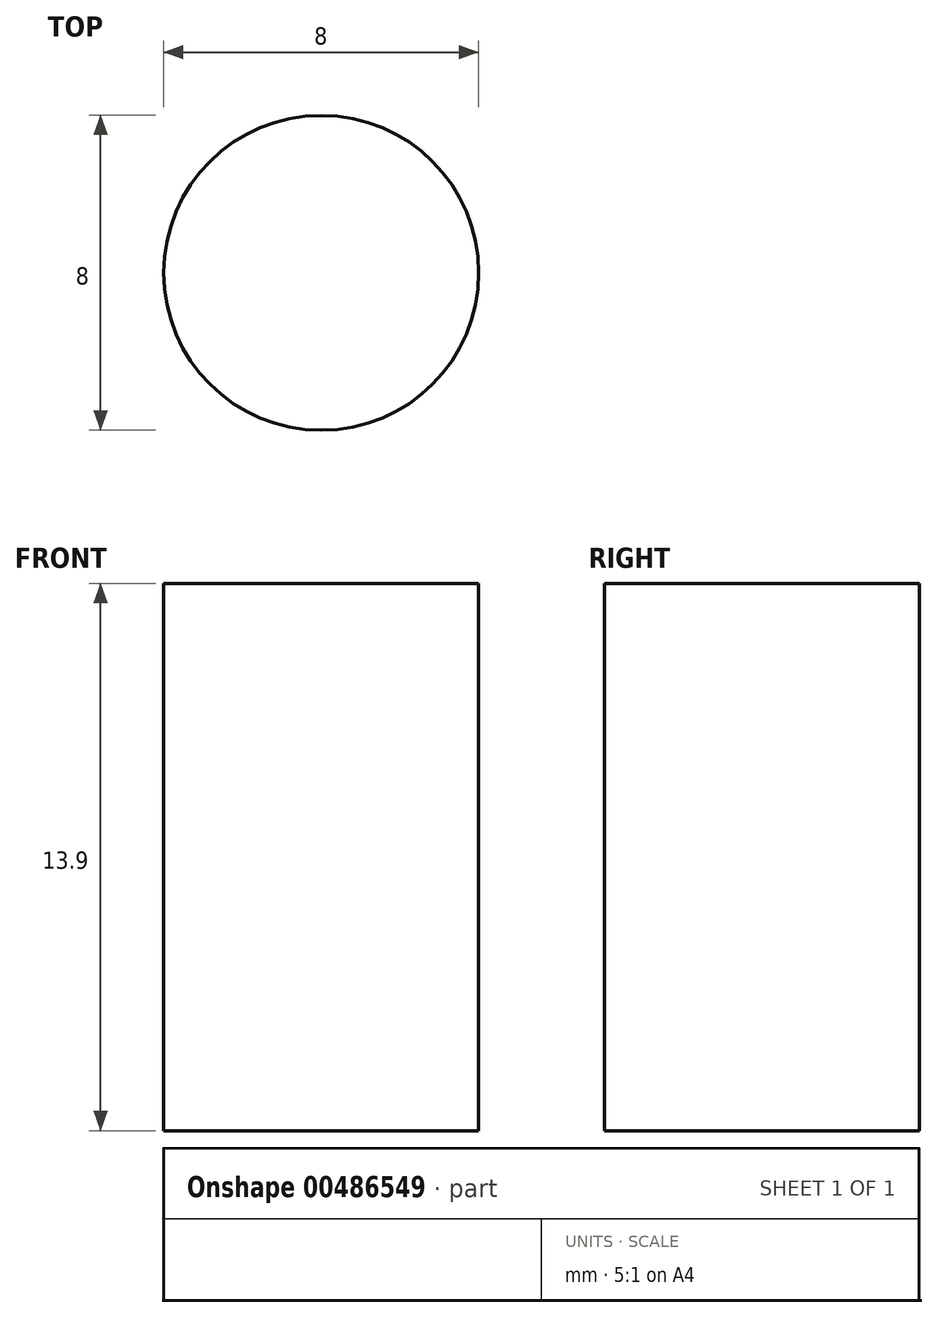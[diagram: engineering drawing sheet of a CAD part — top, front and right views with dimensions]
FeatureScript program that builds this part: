
annotation { "Feature Type Name" : "Feature", "Feature Type Description" : "" }
export const myFeature = defineFeature(function(context is Context, id is Id, definition is map)
    precondition{}
    {
        {
            var Q0;
            Q0=qCreatedBy(makeId("Top.planeOp"),FACE);
            var sketch = newSketch(context, id + "F0", { "sketchPlane" : qUnion([Q0])});
            skCircle(sketch, "E0", {"center": v(-9.17, 13.15) * mm, "radius": 4 * mm});
            skSolve(sketch);
        }
        {
            var Q0;
            Q0=makeQuery(id+"F0.imprint","IMPRINT",FACE,{"disambiguationData":[TD([[makeQuery(id+"F0.imprint","IMPRINT",EDGE,{"derivedFrom":sQuery(id+"F0.wireOp",EDGE,"E0")}),1.0]])]});
            extrude(context, id + "F1", {"entities" : qUnion([Q0]), "depth" : 13.9 * mm, "offsetDistance" : 25 * mm});
        }
    });
